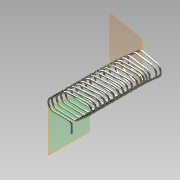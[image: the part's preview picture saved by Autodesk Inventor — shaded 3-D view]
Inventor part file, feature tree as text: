
AUTODESK INVENTOR PART (.ipt)
format: ipt  version: unknown  size: 1,634,304 bytes
history: native  units: mm
features: sketch x8, other x5, extrude x2, reference x2, sweep x1, revolve x1
ambient origin geometry x8: Origin, YZ Plane, XZ Plane, XY Plane, X Axis, Y Axis, Z Axis, Center Point
feature tree (19):
  sketch  "Эскиз1"
  other  "РабПлоскость1"
  sketch  "3D эскиз1"
  other  "РабПлоскость2"
  sweep  "Сдвиг1"
  extrude  "Выдавливание1"  Depth=6.0mm
  revolve  "Вращение1"
  extrude  "Выдавливание2"  Depth=5.0mm
  reference  "Ссылка2"
  reference  "Ссылка3"
  sketch  "Эскиз2"
  sketch  "Эскиз3"
  sketch  "Эскиз4"
  sketch  "Эскиз5"
  sketch  "Эскиз6"
  sketch  "Эскиз7"
  other  "СдвигПврх1"
  other  "ВыдавПврх1"
  other  "3D пересечение1"
